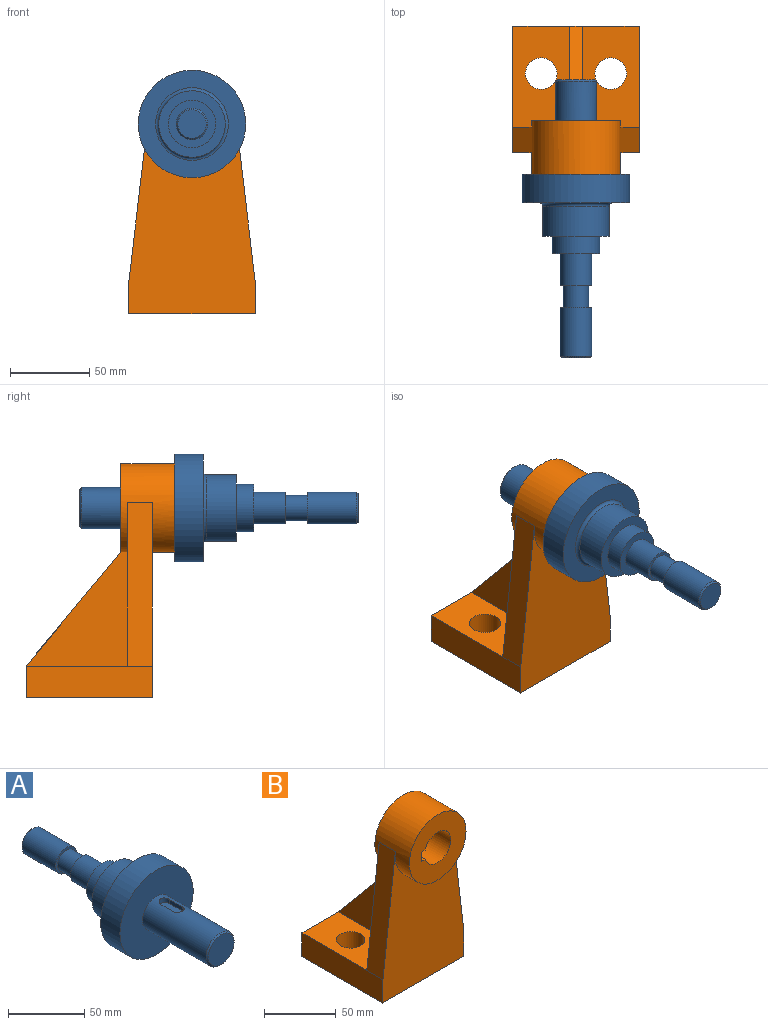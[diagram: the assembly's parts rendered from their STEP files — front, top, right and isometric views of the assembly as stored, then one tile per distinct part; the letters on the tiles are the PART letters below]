
ASSEMBLY  parts=2 mates=1
PART A: 23 faces, bbox 68x176x68 mm
  f0: plane 20x20mm, normal (0,1,0), area 113.1mm2, adj f10,f11
  f1: plane 30x30mm, normal (0,1,0), area 392.7mm2, adj f9,f10
  f2: plane 42x42mm, normal (0,1,0), area 678.6mm2, adj f8,f9
  f3: plane 68x68mm, normal (0,1,0), area 1969.8mm2, adj f6,f22
  f4: cylinder r=13mm len=59mm, axis (0,-1,0), area 4670.7mm2, adj f7,f16,f17,f18,f19,f20
  f5: plane 24x24mm, normal (0,-1,0), area 452.4mm2, adj f16
  f6: cylinder r=34mm len=68mm, axis (0,-1,0), area 3845.3mm2, adj f3,f7
  f7: plane 68x68mm, normal (0,-1,0), area 3100.8mm2, adj f4,f6
  f8: cylinder r=21mm len=42mm, axis (0,-1,0), area 2507mm2, adj f2,f22
  f9: cylinder r=15mm len=30mm, axis (0,-1,0), area 1036.7mm2, adj f1,f2
  f10: cylinder r=10mm len=20mm, axis (0,-1,0), area 1256.6mm2, adj f0,f1
  f11: cylinder r=8mm len=16mm, axis (0,-1,0), area 703.7mm2, adj f0,f12
  f12: plane 20x20mm, normal (0,-1,0), area 113.1mm2, adj f11,f13
  f13: cylinder r=10mm len=31mm, axis (0,-1,0), area 1947.8mm2, adj f12,f15
  f14: plane 18x18mm, normal (0,1,0), area 254.5mm2, adj f15
  f15: cone r=9mm half-angle=45deg, axis (0,-1,0), area 84.4mm2, adj f13,f14
  f16: cone r=12mm half-angle=45deg, axis (0,1,0), area 111.1mm2, adj f4,f5
  f17: cylinder r=4mm len=8mm, axis (0,0,1), area 46.3mm2, adj f4,f18,f20,f21
  f18: plane 12x3.37mm, normal (-1,0,0), area 40.4mm2, adj f4,f17,f19,f21
  f19: cylinder r=4mm len=8mm, axis (0,0,1), area 46.3mm2, adj f4,f18,f20,f21
  f20: plane 12x3.37mm, normal (1,0,0), area 40.4mm2, adj f4,f17,f19,f21
  f21: plane 20x8mm, normal (0,0,1), area 146.3mm2, adj f17,f18,f19,f20
  f22: torus R=23mm, axis (0,1,0), area 428.9mm2, adj f3,f8
PART B: 24 faces, bbox 80x94x148 mm
  f0: plane 103.28x36mm, normal (0,1,0), area 2505.8mm2, adj f1,f9,f12,f21
  f1: plane 64x36mm, normal (0,0,1), area 1989.8mm2, adj f0,f6,f7,f21,f23
  f2: plane 103.28x36mm, normal (0,1,0), area 2505.8mm2, adj f4,f9,f10,f11,f20
  f3: plane 123.28x80mm, normal (0,-1,0), area 7188.4mm2, adj f5,f7,f8,f9,f11,f12
  f4: plane 64x36mm, normal (0,0,1), area 1989.8mm2, adj f2,f5,f6,f20,f22
  f5: plane 80x20mm, normal (1,0,0), area 1600mm2, adj f3,f4,f6,f8,f11
  f6: plane 80x20mm, normal (0,1,0), area 1600mm2, adj f1,f4,f5,f7,f8,f19
  f7: plane 80x20mm, normal (-1,0,0), area 1600mm2, adj f1,f3,f6,f8,f12
  f8: plane 80x80mm, normal (0,0,-1), area 5771.7mm2, adj f3,f5,f6,f7,f22,f23
  f9: cylinder r=28mm len=56mm, axis (0,-1,0), area 4277.2mm2, adj f0,f2,f3,f10,f11,f12,f13,f14
  f10: cylinder r=28mm len=28mm, axis (0,-1,0), area 160.2mm2, adj f2,f9,f14,f19,f20
  f11: plane 103.28x16mm, normal (0.99,0,0.12), area 1664mm2, adj f2,f3,f5,f9
  f12: plane 103.28x16mm, normal (-0.99,0,0.12), area 1664mm2, adj f0,f3,f7,f9
  f13: plane 56x56mm, normal (0,-1,0), area 1904mm2, adj f9,f15,f16,f17,f18
  f14: plane 56x56mm, normal (0,1,0), area 1904mm2, adj f9,f10,f15,f16,f17,f18
  f15: cylinder r=13mm len=34mm, axis (0,-1,0), area 2500.7mm2, adj f13,f14,f17,f18
  f16: plane 34x8mm, normal (1,0,0), area 272mm2, adj f13,f14,f17,f18
  f17: plane 34x3.93mm, normal (0,0,-1), area 133.6mm2, adj f13,f14,f15,f16
  f18: plane 34x3.93mm, normal (0,0,1), area 133.6mm2, adj f13,f14,f15,f16
  f19: plane 72.29x60.24mm, normal (0,0.77,0.64), area 750.8mm2, adj f6,f9,f10,f20,f21
  f20: plane 72.29x64mm, normal (1,0,0), area 2449.1mm2, adj f2,f4,f10,f19
  f21: plane 72.29x64mm, normal (-1,0,0), area 2449.1mm2, adj f0,f1,f9,f19
  f22: cylinder r=10mm len=20mm, axis (0,0,1), area 1256.6mm2, adj f4,f8
  f23: cylinder r=10mm len=20mm, axis (0,0,1), area 1256.6mm2, adj f1,f8
PLACE A rot(axis=(0.67,0,-0.74),180deg) t=(8.97,27.99,60.71)mm
PLACE B t=(8.97,21.99,-59.29)mm fixed
MATE revolute A.f4 <-> B.f9  axis (0,1,0) through (8.97,-32.01,60.71)mm
